FCSTD DOCUMENT  (FreeCAD 0.20R26155 (Git))
Label: SNES_logictop
License: All rights reserved
LicenseURL: http://en.wikipedia.org/wiki/All_rights_reserved
objects: Sketcher::SketchObject×1, PartDesign::Body×1
note: 2 computed .brp shape members not serialized (recipe doc carries the construction recipe); baked Part::Feature solids carry a one-line shape summary decoded from their .brp

FEATURE [Sketcher::SketchObject] Sketch  label="Edge_Cuts_0.1"
  FullyConstrained = true
  MapMode = 5
  Support = -> [XY_Plane]
  sketch-geometry (9):
    g0: LineSegment StartX=96 StartY=5 StartZ=0 EndX=96 EndY=70 EndZ=0
    g1: LineSegment StartX=91 StartY=75 StartZ=0 EndX=-1 EndY=75 EndZ=0
    g2: LineSegment StartX=-6 StartY=70 StartZ=0 EndX=-6 EndY=5 EndZ=0
    g3: ArcOfCircle CenterX=-1 CenterY=70 CenterZ=0 NormalX=0 NormalY=0 NormalZ=1 AngleXU=0 Radius=5 StartAngle=1.5708 EndAngle=3.14159
    g4: ArcOfCircle CenterX=91 CenterY=70 CenterZ=0 NormalX=0 NormalY=0 NormalZ=1 AngleXU=0 Radius=5 StartAngle=1.8388e-12 EndAngle=1.5708
    g5: LineSegment StartX=-6 StartY=5 StartZ=0 EndX=0 EndY=5 EndZ=0
    g6: LineSegment StartX=0 StartY=5 StartZ=0 EndX=0 EndY=0 EndZ=0
    g7: LineSegment StartX=96 StartY=5 StartZ=0 EndX=90 EndY=5 EndZ=0
    g8: LineSegment StartX=90 StartY=5 StartZ=0 EndX=90 EndY=0 EndZ=0
  constraints (25):
    c: Horizontal(g1)
    c: Vertical(g0)
    c: Vertical(g2)
    c: Tangent(g2,g3) = -1.5708
    c: Tangent(g1,g3) = -1.5708
    c: Tangent(g1,g4) = -1.5708
    c: Tangent(g0,g4) = -1.5708
    c: Equal(g3,g4)
    c: Radius(g3) = 5
    c: DistanceX(g2,g0) = 102
    c: Coincident(g2,g5)
    c: PointOnObject(g5,g-2)
    c: Horizontal(g5)
    c: Coincident(g5,g6)
    c: Coincident(g6,g-1)
    c: Coincident(g0,g7)
    c: Horizontal(g7)
    c: Coincident(g7,g8)
    c: PointOnObject(g8,g-1)
    c: Vertical(g8)
    c: Equal(g7,g5)
    c: Equal(g8,g6)
    c: DistanceX(g5,g7) = 90
    c: DistanceY(g6,g6) = 5
    c: DistanceY(g0,g0) = 65
FEATURE [PartDesign::Body] Body
  Group = -> [Sketch]
  Origin = -> Origin
